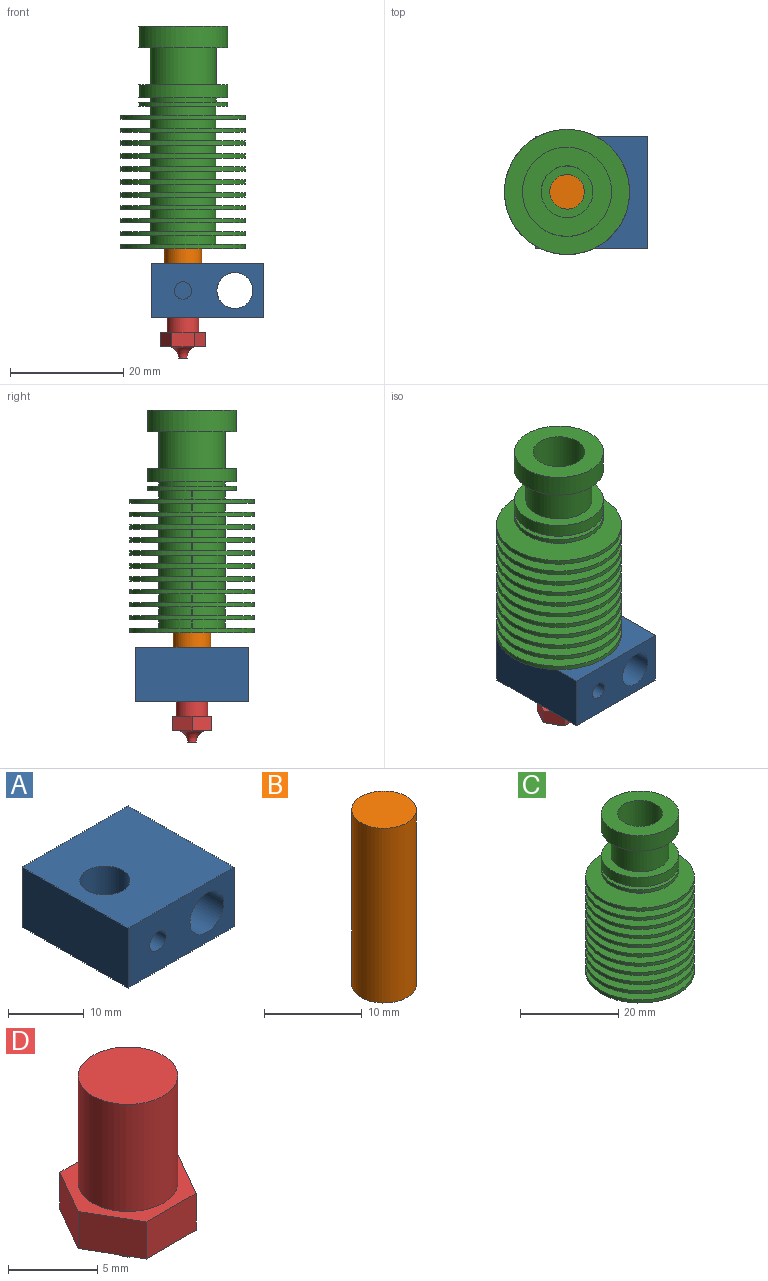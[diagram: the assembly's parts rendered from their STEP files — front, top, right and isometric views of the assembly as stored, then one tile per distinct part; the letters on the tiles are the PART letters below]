
ASSEMBLY  parts=4 mates=3
PART A: 10 faces, bbox 19.8x19.8x9.7 mm
  f0: plane 19.81x9.65mm, normal (-1,0,0), area 191.2mm2, adj f1,f3,f5,f6
  f1: plane 19.81x9.65mm, normal (0,1,0), area 159.6mm2, adj f0,f2,f5,f6,f9
  f2: plane 19.81x9.65mm, normal (1,0,0), area 191.2mm2, adj f1,f3,f5,f6
  f3: plane 19.81x9.65mm, normal (0,-1,0), area 152.3mm2, adj f0,f2,f5,f6,f7,f9
  f4: cylinder r=3.3mm len=9.65mm, axis (0,0,-1), area 200.3mm2, adj f5,f6
  f5: plane 19.81x19.81mm, normal (0,0,1), area 358.3mm2, adj f0,f1,f2,f3,f4
  f6: plane 19.81x19.81mm, normal (0,0,-1), area 358.3mm2, adj f0,f1,f2,f3,f4
  f7: cylinder r=1.52mm len=5.33mm, axis (0,-1,0), area 51.1mm2, adj f3,f8
  f8: plane 3.05x3.05mm, normal (0,-1,0), area 7.3mm2, adj f7
  f9: cylinder r=3.17mm len=19.81mm, axis (0,-1,0), area 395.2mm2, adj f1,f3
PART B: 3 faces, bbox 6.6x6.6x21.8 mm
  f0: cylinder r=3.3mm len=21.84mm, axis (0,0,-1), area 453.2mm2, adj f1,f2
  f1: plane 6.6x6.6mm, normal (0,0,1), area 34.3mm2, adj f0
  f2: plane 6.6x6.6mm, normal (0,0,-1), area 34.3mm2, adj f0
PART C: 91 faces, bbox 22.1x22.1x39.4 mm
  f0: cylinder r=7.87mm len=15.75mm, axis (0,0,-1), area 188.5mm2, adj f2,f4
  f1: cylinder r=4.57mm len=10.41mm, axis (0,0,-1), area 299.2mm2, adj f2,f5
  f2: plane 15.75x15.75mm, normal (0,0,1), area 129.1mm2, adj f0,f1
  f3: cylinder r=5.84mm len=11.68mm, axis (0,0,-1), area 242.4mm2, adj f4,f8
  f4: plane 15.75x15.75mm, normal (0,0,-1), area 87.6mm2, adj f0,f3
  f5: plane 9.14x9.14mm, normal (0,0,1), area 36.5mm2, adj f1,f9
  f6: cylinder r=7.87mm len=15.75mm, axis (0,0,1), area 113.1mm2, adj f7,f8
  f7: plane 15.75x15.75mm, normal (0,0,-1), area 87.6mm2, adj f6,f10
  f8: plane 15.75x15.75mm, normal (0,0,1), area 87.6mm2, adj f3,f6
  f9: cylinder r=3.05mm len=28.96mm, axis (0,0,1), area 554.5mm2, adj f5,f35
  f10: cylinder r=5.84mm len=11.68mm, axis (0,0,1), area 28mm2, adj f7,f33
  f11: plane 1.52x0.13mm, normal (1,0,0), area 0.2mm2, adj f36,f37,f58,f79
  f12: plane 1.52x0.13mm, normal (1,0,0), area 0.2mm2, adj f38,f39,f59,f78
  f13: plane 1.52x0.13mm, normal (1,0,0), area 0.2mm2, adj f40,f41,f60,f77
  f14: plane 1.52x0.13mm, normal (1,0,0), area 0.2mm2, adj f42,f43,f61,f76
  f15: plane 1.52x0.13mm, normal (1,0,0), area 0.2mm2, adj f44,f45,f62,f75
  f16: plane 1.52x0.13mm, normal (1,0,0), area 0.2mm2, adj f46,f47,f63,f74
  f17: plane 1.52x0.13mm, normal (1,0,0), area 0.2mm2, adj f48,f49,f64,f73
  f18: plane 1.52x0.13mm, normal (1,0,0), area 0.2mm2, adj f50,f51,f65,f72
  f19: plane 1.52x0.13mm, normal (1,0,0), area 0.2mm2, adj f52,f53,f66,f71
  f20: plane 1.52x0.13mm, normal (1,0,0), area 0.2mm2, adj f54,f55,f67,f70
  f21: plane 1.52x0.13mm, normal (1,0,0), area 0.2mm2, adj f56,f57,f68,f69
  f22: plane 1.52x0.13mm, normal (-1,0,0), area 0.2mm2, adj f36,f37,f58,f79
  f23: plane 1.52x0.13mm, normal (-1,0,0), area 0.2mm2, adj f38,f39,f59,f78
  f24: plane 1.52x0.13mm, normal (-1,0,0), area 0.2mm2, adj f40,f41,f60,f77
  f25: plane 1.52x0.13mm, normal (-1,0,0), area 0.2mm2, adj f42,f43,f61,f76
  f26: plane 1.52x0.13mm, normal (-1,0,0), area 0.2mm2, adj f44,f45,f62,f75
  f27: plane 1.52x0.13mm, normal (-1,0,0), area 0.2mm2, adj f46,f47,f63,f74
  f28: plane 1.52x0.13mm, normal (-1,0,0), area 0.2mm2, adj f48,f49,f64,f73
  f29: plane 1.52x0.13mm, normal (-1,0,0), area 0.2mm2, adj f50,f51,f65,f72
  f30: plane 1.52x0.13mm, normal (-1,0,0), area 0.2mm2, adj f52,f53,f66,f71
  f31: plane 1.52x0.13mm, normal (-1,0,0), area 0.2mm2, adj f54,f55,f67,f70
  f32: plane 1.52x0.13mm, normal (-1,0,0), area 0.2mm2, adj f56,f57,f68,f69
  f33: plane 15.75x15.75mm, normal (0,0,1), area 87.6mm2, adj f10,f34
  f34: cylinder r=7.87mm len=15.75mm, axis (0,0,1), area 37.7mm2, adj f33,f56
  f35: plane 22.1x22.1mm, normal (0,0,-1), area 354.3mm2, adj f9,f90
  f36: plane 22.1x22.1mm, normal (0,0,-1), area 275.8mm2, adj f11,f22,f58,f79,f89
  f37: plane 22.1x22.1mm, normal (0,0,1), area 275.8mm2, adj f11,f22,f58,f79,f90
  f38: plane 22.1x22.1mm, normal (0,0,-1), area 275.8mm2, adj f12,f23,f59,f78,f88
  f39: plane 22.1x22.1mm, normal (0,0,1), area 275.8mm2, adj f12,f23,f59,f78,f89
  f40: plane 22.1x22.1mm, normal (0,0,-1), area 275.8mm2, adj f13,f24,f60,f77,f87
  f41: plane 22.1x22.1mm, normal (0,0,1), area 275.8mm2, adj f13,f24,f60,f77,f88
  f42: plane 22.1x22.1mm, normal (0,0,-1), area 275.8mm2, adj f14,f25,f61,f76,f86
  f43: plane 22.1x22.1mm, normal (0,0,1), area 275.8mm2, adj f14,f25,f61,f76,f87
  f44: plane 22.1x22.1mm, normal (0,0,-1), area 275.8mm2, adj f15,f26,f62,f75,f85
  f45: plane 22.1x22.1mm, normal (0,0,1), area 275.8mm2, adj f15,f26,f62,f75,f86
  f46: plane 22.1x22.1mm, normal (0,0,-1), area 275.8mm2, adj f16,f27,f63,f74,f84
  f47: plane 22.1x22.1mm, normal (0,0,1), area 275.8mm2, adj f16,f27,f63,f74,f85
  f48: plane 22.1x22.1mm, normal (0,0,-1), area 275.8mm2, adj f17,f28,f64,f73,f83
  f49: plane 22.1x22.1mm, normal (0,0,1), area 275.8mm2, adj f17,f28,f64,f73,f84
  f50: plane 22.1x22.1mm, normal (0,0,-1), area 275.8mm2, adj f18,f29,f65,f72,f82
  f51: plane 22.1x22.1mm, normal (0,0,1), area 275.8mm2, adj f18,f29,f65,f72,f83
  f52: plane 22.1x22.1mm, normal (0,0,-1), area 275.8mm2, adj f19,f30,f66,f71,f81
  f53: plane 22.1x22.1mm, normal (0,0,1), area 275.8mm2, adj f19,f30,f66,f71,f82
  f54: plane 22.1x22.1mm, normal (0,0,-1), area 275.8mm2, adj f20,f31,f67,f70,f80
  f55: plane 22.1x22.1mm, normal (0,0,1), area 275.8mm2, adj f20,f31,f67,f70,f81
  f56: plane 15.75x15.75mm, normal (0,0,-1), area 87mm2, adj f21,f32,f34,f68,f69
  f57: plane 22.1x22.1mm, normal (0,0,1), area 275.8mm2, adj f21,f32,f68,f69,f80
  f58: cylinder r=5.82mm len=11.63mm, axis (0,0,-1), area 27.8mm2, adj f11,f22,f36,f37
  f59: cylinder r=5.82mm len=11.63mm, axis (0,0,-1), area 27.8mm2, adj f12,f23,f38,f39
  f60: cylinder r=5.82mm len=11.63mm, axis (0,0,-1), area 27.8mm2, adj f13,f24,f40,f41
  f61: cylinder r=5.82mm len=11.63mm, axis (0,0,-1), area 27.8mm2, adj f14,f25,f42,f43
  f62: cylinder r=5.82mm len=11.63mm, axis (0,0,-1), area 27.8mm2, adj f15,f26,f44,f45
  f63: cylinder r=5.82mm len=11.63mm, axis (0,0,-1), area 27.8mm2, adj f16,f27,f46,f47
  f64: cylinder r=5.82mm len=11.63mm, axis (0,0,-1), area 27.8mm2, adj f17,f28,f48,f49
  f65: cylinder r=5.82mm len=11.63mm, axis (0,0,-1), area 27.8mm2, adj f18,f29,f50,f51
  f66: cylinder r=5.82mm len=11.63mm, axis (0,0,-1), area 27.8mm2, adj f19,f30,f52,f53
  f67: cylinder r=5.82mm len=11.63mm, axis (0,0,-1), area 27.8mm2, adj f20,f31,f54,f55
  f68: cylinder r=5.82mm len=11.63mm, axis (0,0,-1), area 27.8mm2, adj f21,f32,f56,f57
  f69: cylinder r=5.82mm len=11.63mm, axis (0,0,-1), area 27.8mm2, adj f21,f32,f56,f57
  f70: cylinder r=5.82mm len=11.63mm, axis (0,0,-1), area 27.8mm2, adj f20,f31,f54,f55
  f71: cylinder r=5.82mm len=11.63mm, axis (0,0,-1), area 27.8mm2, adj f19,f30,f52,f53
  f72: cylinder r=5.82mm len=11.63mm, axis (0,0,-1), area 27.8mm2, adj f18,f29,f50,f51
  f73: cylinder r=5.82mm len=11.63mm, axis (0,0,-1), area 27.8mm2, adj f17,f28,f48,f49
  f74: cylinder r=5.82mm len=11.63mm, axis (0,0,-1), area 27.8mm2, adj f16,f27,f46,f47
  f75: cylinder r=5.82mm len=11.63mm, axis (0,0,-1), area 27.8mm2, adj f15,f26,f44,f45
  f76: cylinder r=5.82mm len=11.63mm, axis (0,0,-1), area 27.8mm2, adj f14,f25,f42,f43
  f77: cylinder r=5.82mm len=11.63mm, axis (0,0,-1), area 27.8mm2, adj f13,f24,f40,f41
  f78: cylinder r=5.82mm len=11.63mm, axis (0,0,-1), area 27.8mm2, adj f12,f23,f38,f39
  f79: cylinder r=5.82mm len=11.63mm, axis (0,0,-1), area 27.8mm2, adj f11,f22,f36,f37
  f80: cylinder r=11.05mm len=22.1mm, axis (0,0,1), area 52.9mm2, adj f54,f57
  f81: cylinder r=11.05mm len=22.1mm, axis (0,0,1), area 52.9mm2, adj f52,f55
  f82: cylinder r=11.05mm len=22.1mm, axis (0,0,1), area 52.9mm2, adj f50,f53
  f83: cylinder r=11.05mm len=22.1mm, axis (0,0,1), area 52.9mm2, adj f48,f51
  f84: cylinder r=11.05mm len=22.1mm, axis (0,0,1), area 52.9mm2, adj f46,f49
  f85: cylinder r=11.05mm len=22.1mm, axis (0,0,1), area 52.9mm2, adj f44,f47
  f86: cylinder r=11.05mm len=22.1mm, axis (0,0,1), area 52.9mm2, adj f42,f45
  f87: cylinder r=11.05mm len=22.1mm, axis (0,0,1), area 52.9mm2, adj f40,f43
  f88: cylinder r=11.05mm len=22.1mm, axis (0,0,1), area 52.9mm2, adj f38,f41
  f89: cylinder r=11.05mm len=22.1mm, axis (0,0,1), area 52.9mm2, adj f36,f39
  f90: cylinder r=11.05mm len=22.1mm, axis (0,0,1), area 52.9mm2, adj f35,f37
PART D: 14 faces, bbox 9.2x9.2x11.9 mm
  f0: cylinder r=2.79mm len=7.37mm, axis (0,0,1), area 129.3mm2, adj f1,f9
  f1: plane 5.59x5.59mm, normal (0,0,1), area 24.5mm2, adj f0
  f2: plane 3.43x2.54mm, normal (0.87,-0.5,0), area 10.1mm2, adj f3,f7,f8,f9
  f3: plane 3.96x2.54mm, normal (0,-1,0), area 10.1mm2, adj f2,f4,f8,f9
  f4: plane 3.43x2.54mm, normal (-0.87,-0.5,0), area 10.1mm2, adj f3,f5,f8,f9
  f5: plane 3.43x2.54mm, normal (-0.87,0.5,0), area 10.1mm2, adj f4,f6,f8,f9
  f6: plane 3.96x2.54mm, normal (0,1,0), area 10.1mm2, adj f5,f7,f8,f9
  f7: plane 3.43x2.54mm, normal (0.87,0.5,0), area 10.1mm2, adj f2,f6,f8,f9
  f8: plane 7.92x6.86mm, normal (0,0,-1), area 16.2mm2, adj f2,f3,f4,f5,f6,f7,f13
  f9: plane 7.92x6.86mm, normal (0,0,1), area 16.2mm2, adj f0,f2,f3,f4,f5,f6,f7
  f10: cylinder r=0.51mm len=2.03mm, axis (0,0,1), area 6.5mm2, adj f11,f12
  f11: plane 1.52x1.52mm, normal (0,0,-1), area 1mm2, adj f10,f13
  f12: plane 1.02x1.02mm, normal (0,0,-1), area 0.8mm2, adj f10
  f13: torus R=2.79mm, axis (0,0,-1), area 30.1mm2, adj f8,f11
PLACE A t=(-25.2,-12.2,19.9)mm
PLACE B t=(-25.2,-12.2,19.65)mm
PLACE C t=(-25.2,-12.2,19.9)mm
PLACE D t=(-25.2,-12.2,19.9)mm
MATE fastened D.f0 <-> B.f0  axis (0,0,1) through (-25.2,-12.2,-16.42)mm
MATE fastened A.f4 <-> B.f0  axis (0,0,-1) through (-25.2,-12.2,-16.42)mm
MATE fastened B.f0 <-> C.f9  axis (0,0,-1) through (-25.2,-12.2,5.42)mm
